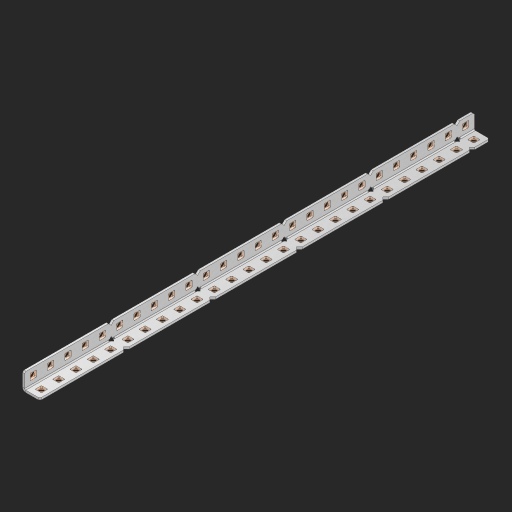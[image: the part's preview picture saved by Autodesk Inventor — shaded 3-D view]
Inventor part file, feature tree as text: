
AUTODESK INVENTOR PART (.ipt)
format: ipt  version: 2023 (Build 270158000, 158)  size: 947,200 bytes
history: native  units: in
note: dims shown in document units (in); Inventor stores cm internally (conversion verified against a paired STEP export)
features: other x58, extrude x53, sheet_metal_op x8, sketch x5, pattern_linear x1, mirror x1, chamfer x1
ambient origin geometry x8: Origin, YZ Plane, XZ Plane, XY Plane, X Axis, Y Axis, Z Axis, Center Point
bodies: Solid1 (feature_tree), Body (feature_tree)
feature tree (127):
  sheet_metal_op  "Flanges"
  sheet_metal_op  "Body Pattern"
  other  "Arc Length"
  pattern_linear  "Notch Pattern"  Spacing1=0.125in  [1 undecoded]
  other  "Diagonal Plane"
  mirror  "Everything Mirrored"
  chamfer  "End Chamfer"
  sketch  "Sketch1"  dims[d0=0.5in]
  other  "Plate1"
  sketch  "Sketch2"  dims[d1=13.0in]
  other  "Plate2"
  sheet_metal_op  "Bend1"
  sheet_metal_op  "Corner1"
  sketch  "Sketch8"  dims[d2=0.0625in]
  sketch  "Sketch9"  dims[d3=0.0625in]
  other  "Srf91"
  sheet_metal_op  "Body Pattern Sketch"
  other  "Srf92"
  sketch  "Sketch13"  dims[d4=0.0312in d5=0.125in d6=0.0625in d7=0.5in d8=90.0deg d9=0.0312in d10=0.25in d11=0.0625in d12=0.0625in d49=0.182in d50=0.02in d52=0.25in d53=0.0625in d54=0.0in d55=0.172in d56=1.0in d57=0.0in d85=0.1473in d86=0.1782in d89=0.0625in d90=0.0in d91=0.04in d92=0.0491in d95=2.5in d96=0.04in d97=0.25in d98=45.0deg d123=0.204in d126=0.0491in d127=0.1473in d128=0.08in d129=0.04in d130=2.5in d131=10.2362in d133=0.5in d134=0.3937in d136=1.0in]
  other  "Srf856"
  other  "Srf857"
  other  "Srf858"
  other  "Srf859"
  other  "Srf860"
  other  "Srf861"
  other  "Srf1275"
  other  "Srf1276"
  other  "Srf1278"
  other  "Srf1279"
  other  "Srf1280"
  other  "Srf1281"
  other  "Srf1282"
  other  "Srf1283"
  other  "Srf1383"
  other  "Srf1384"
  other  "Srf1385"
  other  "Srf1386"
  other  "Srf1387"
  other  "Srf1388"
  other  "Srf1389"
  other  "Srf1390"
  other  "Srf1391"
  other  "Srf1392"
  other  "Srf1393"
  other  "Srf1394"
  other  "Srf1395"
  other  "Srf1396"
  other  "Srf1397"
  other  "Srf1398"
  other  "Srf1399"
  other  "Srf1400"
  other  "Srf1401"
  other  "Srf1475"
  other  "Srf1476"
  other  "Srf1477"
  other  "Srf1478"
  other  "Srf1479"
  other  "Srf1480"
  other  "Srf1481"
  other  "Srf1482"
  other  "Srf1483"
  other  "Srf1484"
  other  "Srf1485"
  other  "Srf1486"
  other  "Srf1487"
  other  "Srf1488"
  other  "Srf1489"
  other  "Srf1490"
  other  "Srf1491"
  other  "Srf1492"
  other  "Srf1493"
  sheet_metal_op  "Body Stamp"
  sheet_metal_op  "Body Circle"
  sheet_metal_op  "Notch"
  extrude  "ExtrusionSrf92"  Depth=0.0625in
  extrude  "ExtrusionSrf856"  Depth=0.5in TaperAngle=90.0deg
  extrude  "ExtrusionSrf857"  Depth=0.25in
  extrude  "ExtrusionSrf858"  Depth=0.0625in
  extrude  "ExtrusionSrf859"  Depth=0.0625in
  extrude  "ExtrusionSrf860"  Depth=0.3937in
  extrude  "ExtrusionSrf861"  Depth=0.02in
  extrude  "ExtrusionSrf1275"  Depth=0.25in
  extrude  "ExtrusionSrf1276"  Depth=0.0625in
  extrude  "ExtrusionSrf1277"  TaperAngle=0.0deg  [1 undecoded]
  extrude  "ExtrusionSrf1278"  Depth=0.3937in
  extrude  "ExtrusionSrf1279"  Depth=0.3937in TaperAngle=0.0deg
  extrude  "ExtrusionSrf1280"  Depth=0.3937in
  extrude  "ExtrusionSrf1281"  Depth=0.3937in
  extrude  "ExtrusionSrf1282"  Depth=0.0625in
  extrude  "ExtrusionSrf1383"  Depth=0.3937in TaperAngle=0.0deg
  extrude  "ExtrusionSrf1384"  Depth=0.3937in
  extrude  "ExtrusionSrf1385"  Depth=0.25in TaperAngle=45.0deg
  extrude  "ExtrusionSrf1386"  Depth=0.3937in
  extrude  "ExtrusionSrf1387"  Depth=0.3937in
  extrude  "ExtrusionSrf1388"  Depth=0.3937in
  extrude  "ExtrusionSrf1389"  Depth=0.3937in
  extrude  "ExtrusionSrf1390"  Depth=0.3937in
  extrude  "ExtrusionSrf1391"  Depth=0.3937in
  extrude  "ExtrusionSrf1392"  Depth=0.3937in
  extrude  "ExtrusionSrf1393"  Depth=0.5in
  extrude  "ExtrusionSrf1394"  [1 undecoded]
  extrude  "ExtrusionSrf1395"  [1 undecoded]
  extrude  "ExtrusionSrf1396"  [1 undecoded]
  extrude  "ExtrusionSrf1397"  [1 undecoded]
  extrude  "ExtrusionSrf1398"  [1 undecoded]
  extrude  "ExtrusionSrf1399"  [1 undecoded]
  extrude  "ExtrusionSrf1400"  [1 undecoded]
  extrude  "ExtrusionSrf1401"  [1 undecoded]
  extrude  "ExtrusionSrf1475"  [1 undecoded]
  extrude  "ExtrusionSrf1476"  [1 undecoded]
  extrude  "ExtrusionSrf1477"  [1 undecoded]
  extrude  "ExtrusionSrf1478"  [1 undecoded]
  extrude  "ExtrusionSrf1479"  [1 undecoded]
  extrude  "ExtrusionSrf1480"  [1 undecoded]
  extrude  "ExtrusionSrf1481"  [1 undecoded]
  extrude  "ExtrusionSrf1482"  [1 undecoded]
  extrude  "ExtrusionSrf1483"  [1 undecoded]
  extrude  "ExtrusionSrf1484"  [1 undecoded]
  extrude  "ExtrusionSrf1485"  [1 undecoded]
  extrude  "ExtrusionSrf1486"  [1 undecoded]
  extrude  "ExtrusionSrf1487"  [1 undecoded]
  extrude  "ExtrusionSrf1488"  [1 undecoded]
  extrude  "ExtrusionSrf1489"  [1 undecoded]
  extrude  "ExtrusionSrf1490"  [1 undecoded]
  extrude  "ExtrusionSrf1491"  [1 undecoded]
  extrude  "ExtrusionSrf1492"  [1 undecoded]
  extrude  "ExtrusionSrf1493"  [1 undecoded]
note: 29 required parameter values undecoded (feature->parameter linkage not recoverable at this tier; creation-order binding heuristic only, values carry confidence <= 0.55)
